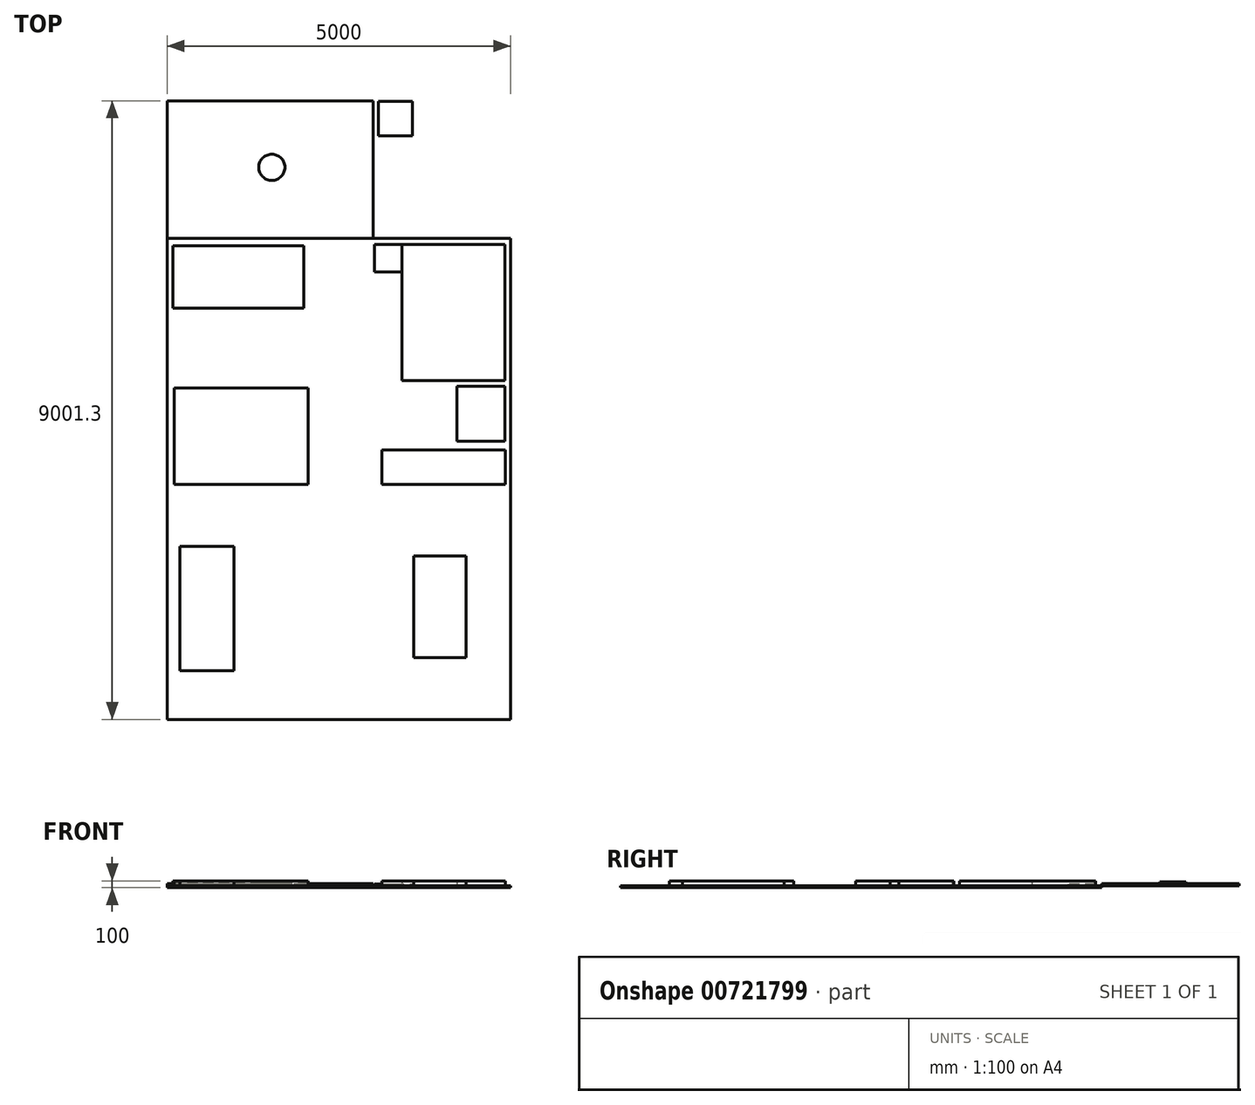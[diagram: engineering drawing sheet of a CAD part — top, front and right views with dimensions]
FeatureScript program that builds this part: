
annotation { "Feature Type Name" : "Feature", "Feature Type Description" : "" }
export const myFeature = defineFeature(function(context is Context, id is Id, definition is map)
    precondition{}
    {
        {
            var Q0;
            Q0=qCreatedBy(makeId("Top.planeOp"),FACE);
            var sketch = newSketch(context, id + "F0", { "sketchPlane" : qUnion([Q0])});
            skLineSegment(sketch, "E0.bottom", {"start": v(7037.15, -3230.18) * mm, "end": v(2037.15, -3230.18) * mm});
            skLineSegment(sketch, "E0.top", {"start": v(7037.15, 3769.82) * mm, "end": v(2037.15, 3769.82) * mm});
            skLineSegment(sketch, "E0.left", {"start": v(7037.15, -3230.18) * mm, "end": v(7037.15, 3769.82) * mm});
            skLineSegment(sketch, "E0.right", {"start": v(2037.15, -3230.18) * mm, "end": v(2037.15, 3769.82) * mm});
            skPoint(sketch, "E0.middle", {"position": v(4537.15, 269.82) * mm});
            skLineSegment(sketch, "E1.bottom", {"start": v(5454.16, 3679.5) * mm, "end": v(6954.16, 3679.5) * mm});
            skLineSegment(sketch, "E1.top", {"start": v(5454.16, 1699.5) * mm, "end": v(6954.16, 1699.5) * mm});
            skLineSegment(sketch, "E1.left", {"start": v(5454.16, 3679.5) * mm, "end": v(5454.16, 1699.5) * mm});
            skLineSegment(sketch, "E1.right", {"start": v(6954.16, 3679.5) * mm, "end": v(6954.16, 1699.5) * mm});
            skLineSegment(sketch, "E2.bottom", {"start": v(5161.35, 691.31) * mm, "end": v(6961.35, 691.31) * mm});
            skLineSegment(sketch, "E2.top", {"start": v(5161.35, 191.31) * mm, "end": v(6961.35, 191.31) * mm});
            skLineSegment(sketch, "E2.left", {"start": v(5161.35, 691.31) * mm, "end": v(5161.35, 191.31) * mm});
            skLineSegment(sketch, "E2.right", {"start": v(6961.35, 691.31) * mm, "end": v(6961.35, 191.31) * mm});
            skLineSegment(sketch, "E3.bottom", {"start": v(2220.77, -2520.39) * mm, "end": v(3010.77, -2520.39) * mm});
            skLineSegment(sketch, "E3.top", {"start": v(2220.77, -710.39) * mm, "end": v(3010.77, -710.39) * mm});
            skLineSegment(sketch, "E3.left", {"start": v(2220.77, -2520.39) * mm, "end": v(2220.77, -710.39) * mm});
            skLineSegment(sketch, "E3.right", {"start": v(3010.77, -2520.39) * mm, "end": v(3010.77, -710.39) * mm});
            skLineSegment(sketch, "E4.bottom", {"start": v(5623.76, -850.18) * mm, "end": v(6383.76, -850.18) * mm});
            skLineSegment(sketch, "E4.top", {"start": v(5623.76, -2330.18) * mm, "end": v(6383.76, -2330.18) * mm});
            skLineSegment(sketch, "E4.left", {"start": v(5623.76, -850.18) * mm, "end": v(5623.76, -2330.18) * mm});
            skLineSegment(sketch, "E4.right", {"start": v(6383.76, -850.18) * mm, "end": v(6383.76, -2330.18) * mm});
            skLineSegment(sketch, "E5.bottom", {"start": v(5054.16, 3679.5) * mm, "end": v(5454.16, 3679.5) * mm});
            skLineSegment(sketch, "E5.top", {"start": v(5054.16, 3279.5) * mm, "end": v(5454.16, 3279.5) * mm});
            skLineSegment(sketch, "E5.left", {"start": v(5054.16, 3679.5) * mm, "end": v(5054.16, 3279.5) * mm});
            skLineSegment(sketch, "E5.right", {"start": v(5454.16, 3679.5) * mm, "end": v(5454.16, 3279.5) * mm});
            skLineSegment(sketch, "E6.bottom", {"start": v(6254.73, 1615.8) * mm, "end": v(6954.73, 1615.8) * mm});
            skLineSegment(sketch, "E6.top", {"start": v(6254.73, 815.8) * mm, "end": v(6954.73, 815.8) * mm});
            skLineSegment(sketch, "E6.left", {"start": v(6254.73, 1615.8) * mm, "end": v(6254.73, 815.8) * mm});
            skLineSegment(sketch, "E6.right", {"start": v(6954.73, 1615.8) * mm, "end": v(6954.73, 815.8) * mm});
            skLineSegment(sketch, "E7.bottom", {"start": v(2139.02, 1591.31) * mm, "end": v(4089.02, 1591.31) * mm});
            skLineSegment(sketch, "E7.top", {"start": v(2139.02, 191.31) * mm, "end": v(4089.02, 191.31) * mm});
            skLineSegment(sketch, "E7.left", {"start": v(2139.02, 1591.31) * mm, "end": v(2139.02, 191.31) * mm});
            skLineSegment(sketch, "E7.right", {"start": v(4089.02, 1591.31) * mm, "end": v(4089.02, 191.31) * mm});
            skLineSegment(sketch, "E8.bottom", {"start": v(2121.34, 3664.53) * mm, "end": v(4021.34, 3664.53) * mm});
            skLineSegment(sketch, "E8.top", {"start": v(2121.34, 2754.53) * mm, "end": v(4021.34, 2754.53) * mm});
            skLineSegment(sketch, "E8.left", {"start": v(2121.34, 3664.53) * mm, "end": v(2121.34, 2754.53) * mm});
            skLineSegment(sketch, "E8.right", {"start": v(4021.34, 3664.53) * mm, "end": v(4021.34, 2754.53) * mm});
            skSolve(sketch);
        }
        {
            var Q0;
            Q0=makeQuery(id+"F0.imprint","IMPRINT",FACE,{"disambiguationData":[TD([[makeQuery(id+"F0.imprint","IMPRINT",EDGE,{"derivedFrom":sQuery(id+"F0.wireOp",EDGE,"E0.bottom")}),-1.0]])]});
            extrude(context, id + "F1", {"entities" : qUnion([Q0]), "depth" : 25 * mm, "offsetDistance" : 25 * mm});
        }
        {
            var Q0;
            Q0=makeQuery(id+"F0.imprint","IMPRINT",FACE,{"disambiguationData":[TD([[makeQuery(id+"F0.imprint","IMPRINT",EDGE,{"derivedFrom":sQuery(id+"F0.wireOp",EDGE,"E8.bottom")}),-1.0]])]});
            extrude(context, id + "F2", {"entities" : qUnion([Q0]), "operationType" : NewBodyOperationType.ADD, "depth" : 100 * mm, "offsetDistance" : 25 * mm});
        }
        {
            var Q0;
            Q0=makeQuery(id+"F0.imprint","IMPRINT",FACE,{"disambiguationData":[TD([[makeQuery(id+"F0.imprint","IMPRINT",EDGE,{"derivedFrom":sQuery(id+"F0.wireOp",EDGE,"E7.bottom")}),-1.0]])]});
            extrude(context, id + "F3", {"entities" : qUnion([Q0]), "operationType" : NewBodyOperationType.ADD, "depth" : 100 * mm, "offsetDistance" : 25 * mm});
        }
        {
            var Q0;
            Q0=makeQuery(id+"F0.imprint","IMPRINT",FACE,{"disambiguationData":[TD([[makeQuery(id+"F0.imprint","IMPRINT",EDGE,{"derivedFrom":sQuery(id+"F0.wireOp",EDGE,"E5.bottom")}),-1.0]])]});
            extrude(context, id + "F4", {"entities" : qUnion([Q0]), "operationType" : NewBodyOperationType.ADD, "depth" : 50 * mm, "offsetDistance" : 25 * mm});
        }
        {
            var Q0;
            Q0=makeQuery(id+"F0.imprint","IMPRINT",FACE,{"disambiguationData":[TD([[makeQuery(id+"F0.imprint","IMPRINT",EDGE,{"derivedFrom":sQuery(id+"F0.wireOp",EDGE,"E1.bottom")}),-1.0]])]});
            extrude(context, id + "F5", {"entities" : qUnion([Q0]), "operationType" : NewBodyOperationType.ADD, "depth" : 100 * mm, "offsetDistance" : 25 * mm});
        }
        {
            var Q0;
            Q0=makeQuery(id+"F0.imprint","IMPRINT",FACE,{"disambiguationData":[TD([[makeQuery(id+"F0.imprint","IMPRINT",EDGE,{"derivedFrom":sQuery(id+"F0.wireOp",EDGE,"E6.bottom")}),-1.0]])]});
            extrude(context, id + "F6", {"entities" : qUnion([Q0]), "operationType" : NewBodyOperationType.ADD, "depth" : 100 * mm, "offsetDistance" : 25 * mm});
        }
        {
            var Q0;
            Q0=makeQuery(id+"F0.imprint","IMPRINT",FACE,{"disambiguationData":[TD([[makeQuery(id+"F0.imprint","IMPRINT",EDGE,{"derivedFrom":sQuery(id+"F0.wireOp",EDGE,"E2.bottom")}),-1.0]])]});
            extrude(context, id + "F7", {"entities" : qUnion([Q0]), "operationType" : NewBodyOperationType.ADD, "depth" : 100 * mm, "offsetDistance" : 25 * mm});
        }
        {
            var Q0;
            Q0=makeQuery(id+"F0.imprint","IMPRINT",FACE,{"disambiguationData":[TD([[makeQuery(id+"F0.imprint","IMPRINT",EDGE,{"derivedFrom":sQuery(id+"F0.wireOp",EDGE,"E4.bottom")}),-1.0]])]});
            extrude(context, id + "F8", {"entities" : qUnion([Q0]), "operationType" : NewBodyOperationType.ADD, "depth" : 100 * mm, "offsetDistance" : 25 * mm});
        }
        {
            var Q0;
            Q0=makeQuery(id+"F0.imprint","IMPRINT",FACE,{"disambiguationData":[TD([[makeQuery(id+"F0.imprint","IMPRINT",EDGE,{"derivedFrom":sQuery(id+"F0.wireOp",EDGE,"E3.bottom")}),1.0]])]});
            extrude(context, id + "F9", {"entities" : qUnion([Q0]), "operationType" : NewBodyOperationType.ADD, "depth" : 100 * mm, "offsetDistance" : 25 * mm});
        }
        {
            var Q0;
            Q0=makeQuery(id+"F1.opExtrude","CAP_FACE",FACE,{"disambiguationData":[OSD([sQuery(id+"F0.wireOp",EDGE,"E0.bottom"),sQuery(id+"F0.wireOp",EDGE,"E0.top"),sQuery(id+"F0.wireOp",EDGE,"E0.left"),sQuery(id+"F0.wireOp",EDGE,"E0.right"),sQuery(id+"F0.wireOp",EDGE,"E1.bottom"),sQuery(id+"F0.wireOp",EDGE,"E1.top"),sQuery(id+"F0.wireOp",EDGE,"E1.left"),sQuery(id+"F0.wireOp",EDGE,"E1.right"),sQuery(id+"F0.wireOp",EDGE,"E2.bottom"),sQuery(id+"F0.wireOp",EDGE,"E2.top"),sQuery(id+"F0.wireOp",EDGE,"E2.left"),sQuery(id+"F0.wireOp",EDGE,"E2.right"),sQuery(id+"F0.wireOp",EDGE,"E3.bottom"),sQuery(id+"F0.wireOp",EDGE,"E3.top"),sQuery(id+"F0.wireOp",EDGE,"E3.left"),sQuery(id+"F0.wireOp",EDGE,"E3.right"),sQuery(id+"F0.wireOp",EDGE,"E4.bottom"),sQuery(id+"F0.wireOp",EDGE,"E4.top"),sQuery(id+"F0.wireOp",EDGE,"E4.left"),sQuery(id+"F0.wireOp",EDGE,"E4.right"),sQuery(id+"F0.wireOp",EDGE,"E5.bottom"),sQuery(id+"F0.wireOp",EDGE,"E5.top"),sQuery(id+"F0.wireOp",EDGE,"E5.left"),sQuery(id+"F0.wireOp",EDGE,"E6.bottom"),sQuery(id+"F0.wireOp",EDGE,"E6.top"),sQuery(id+"F0.wireOp",EDGE,"E6.left"),sQuery(id+"F0.wireOp",EDGE,"E6.right"),sQuery(id+"F0.wireOp",EDGE,"E7.bottom"),sQuery(id+"F0.wireOp",EDGE,"E7.top"),sQuery(id+"F0.wireOp",EDGE,"E7.left"),sQuery(id+"F0.wireOp",EDGE,"E7.right"),sQuery(id+"F0.wireOp",EDGE,"E8.bottom"),sQuery(id+"F0.wireOp",EDGE,"E8.top"),sQuery(id+"F0.wireOp",EDGE,"E8.left"),sQuery(id+"F0.wireOp",EDGE,"E8.right")])],"isStart":false});
            var sketch = newSketch(context, id + "F10", { "sketchPlane" : qUnion([Q0])});
            skLineSegment(sketch, "E9.bottom", {"start": v(2037.15, 3769.82) * mm, "end": v(5037.15, 3769.82) * mm});
            skLineSegment(sketch, "E9.top", {"start": v(2037.15, 5769.82) * mm, "end": v(5037.15, 5769.82) * mm});
            skLineSegment(sketch, "E9.left", {"start": v(2037.15, 3769.82) * mm, "end": v(2037.15, 5769.82) * mm});
            skLineSegment(sketch, "E9.right", {"start": v(5037.15, 3769.82) * mm, "end": v(5037.15, 5769.82) * mm});
            skSolve(sketch);
        }
        {
            var Q0;
            {var subQ39=sQuery(id+"F10.wireOp",EDGE,"E9.bottom");Q0=makeQuery(id+"F10.imprint","IMPRINT",FACE,{"disambiguationData":[TD([[makeQuery(id+"F10.imprint","IMPRINT",EDGE,{"derivedFrom":subQ39}),1.0]])]});}
            var sketch = newSketch(context, id + "F11", { "sketchPlane" : qUnion([Q0])});
            skLineSegment(sketch, "E10.bottom", {"start": v(5107.72, 5765.89) * mm, "end": v(5607.72, 5765.89) * mm});
            skLineSegment(sketch, "E10.top", {"start": v(5107.72, 5265.89) * mm, "end": v(5607.72, 5265.89) * mm});
            skLineSegment(sketch, "E10.left", {"start": v(5107.72, 5765.89) * mm, "end": v(5107.72, 5265.89) * mm});
            skLineSegment(sketch, "E10.right", {"start": v(5607.72, 5765.89) * mm, "end": v(5607.72, 5265.89) * mm});
            skSolve(sketch);
        }
        {
            var Q0;
            {var subQ39=sQuery(id+"F10.wireOp",EDGE,"E9.bottom");Q0=makeQuery(id+"F11.imprint","IMPRINT",FACE,{"disambiguationData":[TD([[makeQuery(id+"F11.imprint","IMPRINT",EDGE,{"derivedFrom":makeQuery(id+"F10.imprint","IMPRINT",EDGE,{"derivedFrom":subQ39})}),1.0]])]});}
            var sketch = newSketch(context, id + "F12", { "sketchPlane" : qUnion([Q0])});
            skCircle(sketch, "E11", {"center": v(3561.71, 4791.15) * mm, "radius": 126.55 * mm});
            skLineSegment(sketch, "E12.bottom", {"start": v(2037.28, 5771.12) * mm, "end": v(3291.26, 5771.12) * mm});
            skLineSegment(sketch, "E12.top", {"start": v(2037.28, 4739.23) * mm, "end": v(3291.26, 4739.23) * mm});
            skLineSegment(sketch, "E12.left", {"start": v(2037.28, 5771.12) * mm, "end": v(2037.28, 4739.23) * mm});
            skLineSegment(sketch, "E12.right", {"start": v(3291.26, 5771.12) * mm, "end": v(3291.26, 4739.23) * mm});
            skLineSegment(sketch, "E13.bottom", {"start": v(2037.28, 4597.54) * mm, "end": v(2534.35, 4597.54) * mm});
            skLineSegment(sketch, "E13.top", {"start": v(2037.28, 3780.03) * mm, "end": v(2534.35, 3780.03) * mm});
            skLineSegment(sketch, "E13.left", {"start": v(2037.28, 4597.54) * mm, "end": v(2037.28, 3780.03) * mm});
            skLineSegment(sketch, "E13.right", {"start": v(2534.35, 4597.54) * mm, "end": v(2534.35, 3780.03) * mm});
            skLineSegment(sketch, "E14.bottom", {"start": v(5035.1, 5628.82) * mm, "end": v(4785.45, 5628.82) * mm});
            skLineSegment(sketch, "E14.top", {"start": v(5035.1, 5159.32) * mm, "end": v(4785.45, 5159.32) * mm});
            skLineSegment(sketch, "E14.left", {"start": v(5035.1, 5628.82) * mm, "end": v(5035.1, 5159.32) * mm});
            skLineSegment(sketch, "E14.right", {"start": v(4785.45, 5628.82) * mm, "end": v(4785.45, 5159.32) * mm});
            skArc(sketch, "E15", {"start": v(4785.45, 5567.05) * mm, "mid": v(4531.68, 5398.55) * mm, "end": v(4785.45, 5230.05) * mm});
            skSolve(sketch);
        }
        {
            var Q0;
            Q0=makeQuery(id+"F10.imprint","IMPRINT",FACE,{"disambiguationData":[TD([[makeQuery(id+"F10.imprint","IMPRINT",EDGE,{"derivedFrom":sQuery(id+"F10.wireOp",EDGE,"E9.bottom")}),-1.0]])]});
            extrude(context, id + "F13", {"entities" : qUnion([Q0]), "depth" : 12.5 * mm, "offsetDistance" : 25 * mm});
        }
        {
            var Q0;
            Q0 = qSketchRegion(id + "F11", true);
            extrude(context, id + "F14", {"entities" : qUnion([Q0]), "depth" : 25 * mm, "offsetDistance" : 25 * mm});
        }
        {
            var Q0;
            Q0 = qSketchRegion(id + "F12", true);
            var Q1;
            Q1=makeQuery(id+"F13.opExtrude","CAP_FACE",FACE,{"disambiguationData":[OSD([sQuery(id+"F10.wireOp",EDGE,"E9.bottom"),sQuery(id+"F10.wireOp",EDGE,"E9.top"),sQuery(id+"F10.wireOp",EDGE,"E9.left"),sQuery(id+"F10.wireOp",EDGE,"E9.right")])],"isStart":false});
            extrude(context, id + "F15", {"entities" : qUnion([Q0, Q1]), "operationType" : NewBodyOperationType.ADD, "depth" : 25 * mm, "offsetDistance" : 25 * mm});
        }
        {
            var Q0;
            Q0=makeQuery(id+"F15.opExtrude","CAP_FACE",FACE,{"disambiguationData":[OSD([sQuery(id+"F10.wireOp",EDGE,"E9.bottom"),sQuery(id+"F10.wireOp",EDGE,"E9.top"),sQuery(id+"F10.wireOp",EDGE,"E9.left"),sQuery(id+"F10.wireOp",EDGE,"E9.right")])],"isStart":false});
            var sketch = newSketch(context, id + "F16", { "sketchPlane" : qUnion([Q0])});
            skCircle(sketch, "E16", {"center": v(3559.02, 4804.9) * mm, "radius": 190.4 * mm});
            skSolve(sketch);
        }
        {
            var Q0;
            Q0=makeQuery(id+"F16.imprint","IMPRINT",FACE,{"disambiguationData":[TD([[makeQuery(id+"F16.imprint","IMPRINT",EDGE,{"derivedFrom":sQuery(id+"F16.wireOp",EDGE,"E16")}),1.0]])]});
            extrude(context, id + "F17", {"entities" : qUnion([Q0]), "operationType" : NewBodyOperationType.ADD, "depth" : 25 * mm, "offsetDistance" : 25 * mm});
        }
    });
